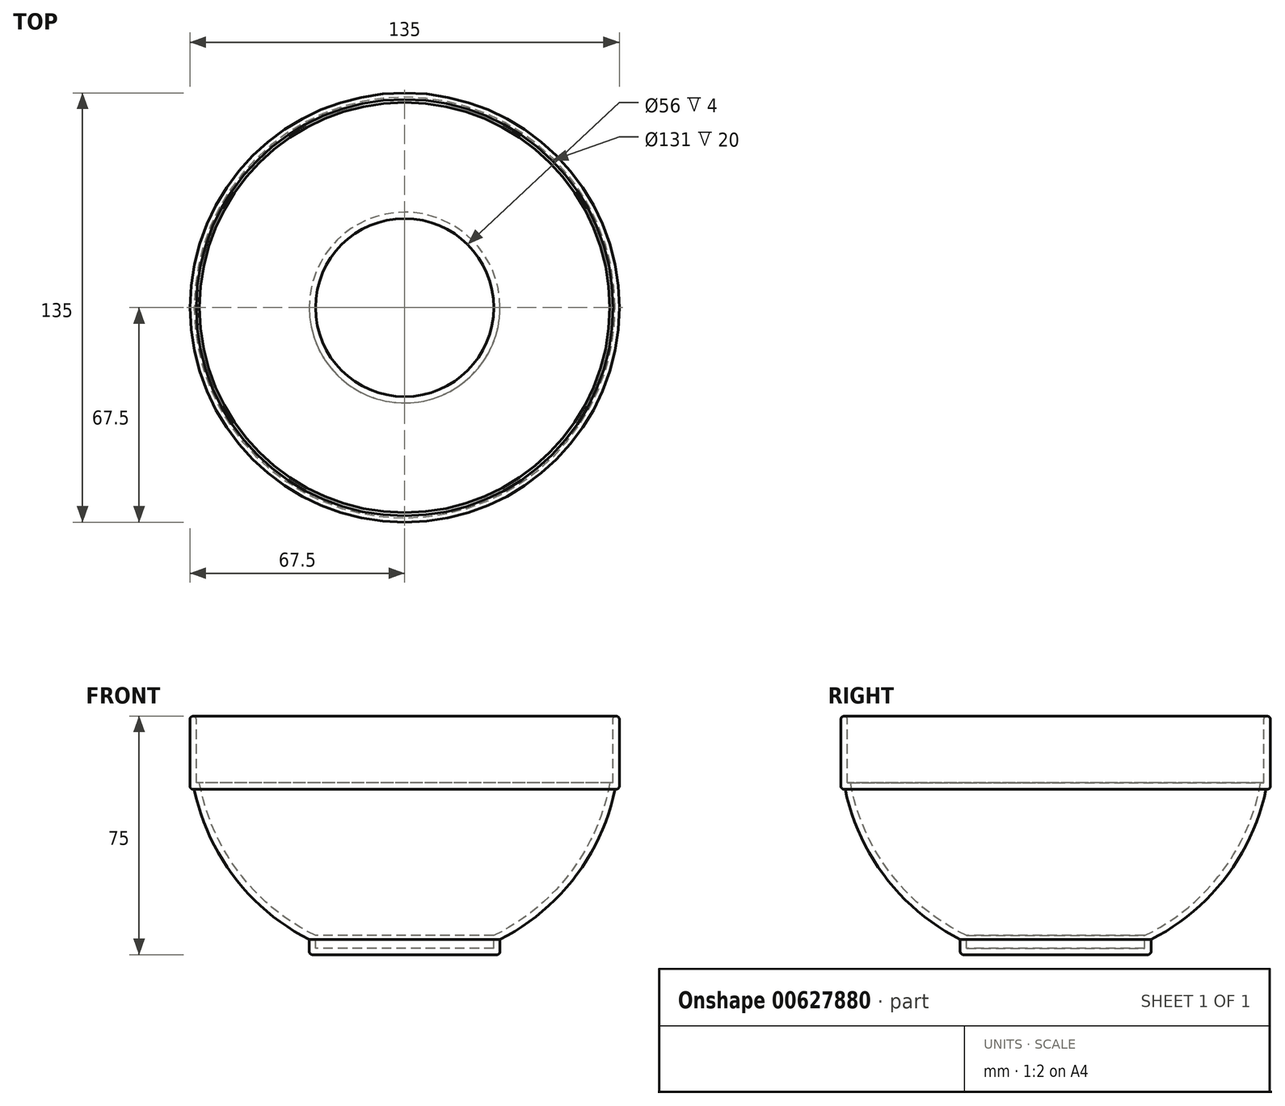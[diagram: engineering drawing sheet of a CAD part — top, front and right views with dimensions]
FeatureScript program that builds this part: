
annotation { "Feature Type Name" : "Feature", "Feature Type Description" : "" }
export const myFeature = defineFeature(function(context is Context, id is Id, definition is map)
    precondition{}
    {
        {
            var Q0;
            Q0=qCreatedBy(makeId("Front.planeOp"),FACE);
            var sketch = newSketch(context, id + "F0", { "sketchPlane" : qUnion([Q0])});
            skLineSegment(sketch, "E0.top", {"start": v(-65.5, 52) * mm, "end": v(-64.5, 52) * mm});
            skLineSegment(sketch, "E0.left", {"start": v(-65.5, 73) * mm, "end": v(-65.5, 52) * mm});
            skLineSegment(sketch, "E1.left", {"start": v(-28, 4) * mm, "end": v(-28, 0) * mm});
            skArc(sketch, "E2", {"start": v(-64.5, 52) * mm, "mid": v(-51.97, 23.65) * mm, "end": v(-28, 4) * mm});
            skLineSegment(sketch, "E3", {"start": v(-28, 0) * mm, "end": v(0, 0) * mm});
            skLineSegment(sketch, "E4.0", {"start": v(-30, -2) * mm, "end": v(0, -2) * mm});
            skLineSegment(sketch, "E4.1", {"start": v(-67.5, 73) * mm, "end": v(-67.5, 50) * mm});
            skLineSegment(sketch, "E4.2", {"start": v(-67.5, 50) * mm, "end": v(-66.14, 50) * mm});
            skArc(sketch, "E4.3", {"start": v(-66.14, 50) * mm, "mid": v(-53.44, 22.27) * mm, "end": v(-30, 2.76) * mm});
            skLineSegment(sketch, "E4.4", {"start": v(-30, 2.76) * mm, "end": v(-30, -2) * mm});
            skLineSegment(sketch, "E5", {"start": v(0, 0) * mm, "end": v(0, -2) * mm});
            skLineSegment(sketch, "E6", {"start": v(-67.5, 73) * mm, "end": v(-65.5, 73) * mm});
            skSolve(sketch);
        }
        {
            var Q0;
            Q0 = qSketchRegion(id + "F0", true);
            var Q1;
            Q1=sQuery(id+"F0.wireOp",EDGE,"E5");
            revolve(context, id + "F1", {"entities" : qUnion([Q0]), "axis" : qUnion([Q1]), "revolveType" : RevolveType.FULL});
        }
        {
            var Q0;
            Q0=makeQuery(id+"F1.opRevolve","SWEPT_EDGE",EDGE,{"disambiguationData":[OSD([sQuery(id+"F0.wireOp",EDGE,"E4.1"),sQuery(id+"F0.wireOp",EDGE,"E6")])]});
            var Q1;
            Q1=makeQuery(id+"F1.opRevolve","SWEPT_EDGE",EDGE,{"disambiguationData":[OSD([sQuery(id+"F0.wireOp",EDGE,"E0.left"),sQuery(id+"F0.wireOp",EDGE,"E6")])]});
            var Q2;
            Q2=makeQuery(id+"F1.opRevolve","SWEPT_EDGE",EDGE,{"disambiguationData":[OSD([sQuery(id+"F0.wireOp",EDGE,"E4.1"),sQuery(id+"F0.wireOp",EDGE,"E4.2")])]});
            var Q3;
            Q3=makeQuery(id+"F1.opRevolve","SWEPT_EDGE",EDGE,{"disambiguationData":[OSD([sQuery(id+"F0.wireOp",EDGE,"E4.0"),sQuery(id+"F0.wireOp",EDGE,"E4.4")])]});
            fillet(context, id + "F2", {"entities" : qUnion([Q0, Q1, Q2, Q3]), "radius" : 1 * mm, "tangentPropagation" : true, "allowEdgeOverflow" : false});
        }
    });
